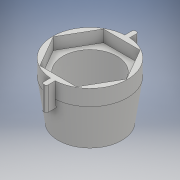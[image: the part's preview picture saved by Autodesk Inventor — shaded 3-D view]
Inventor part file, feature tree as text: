
AUTODESK INVENTOR PART (.ipt)
format: ipt  version: 2017 (Build 210142000, 142)  size: 172,032 bytes
history: native  units: mm
features: other x4, extrude x3, sketch x3, direct_edit x2, hole x1, chamfer x1, reference x1, move_body x1
ambient origin geometry x8: Origin, YZ Plane, XZ Plane, XY Plane, X Axis, Y Axis, Z Axis, Center Point
bodies: Solid1 (feature_tree)
feature tree (16):
  extrude  "Extrusion1"  Depth=0.25mm
  extrude  "Extrusion2"  Depth=8.0mm
  hole  "Hole1"  [1 undecoded]
  direct_edit  "Direct Edit1"
  direct_edit  "Direct Edit2"
  extrude  "Extrusion3"  [1 undecoded]
  chamfer  "Chamfer1"  Distance=4.0mm
  sketch  "Sketch1"  dims[d2=0.2mm d3=0.25mm]
  sketch  "Sketch2"  dims[d4=3.0mm d5=0.0mm d6=8.0mm]
  reference  "Reference9"
  sketch  "Sketch4"  dims[d7=1.0mm d8=0.0mm d21=10.0mm d22=10.0mm d11=6.8mm d12=6.0mm d13=4.0mm d14=2.0mm d15=90.0deg d16=8.0mm d17=20.594885mm d18=0.0mm d19=0.0mm d20=-0.5mm d23=-0.1mm d26=4.0mm d27=0.0mm d28=0.7mm d29=5.0mm d30=45.0deg]
  parser-record x1  (decoder bookkeeping rows leaked as tree rows — omitted from the tree; the rows remain in map.json)
  other  "assembly_full.iam"
  other  "base:1"
  move_body  "Move1"
  other  "Size1"
note: 2 required parameter values undecoded (feature->parameter linkage not recoverable at this tier; creation-order binding heuristic only, values carry confidence <= 0.55)
note: 1 file-system path scrubbed to <path> (originals preserved in map.json)
